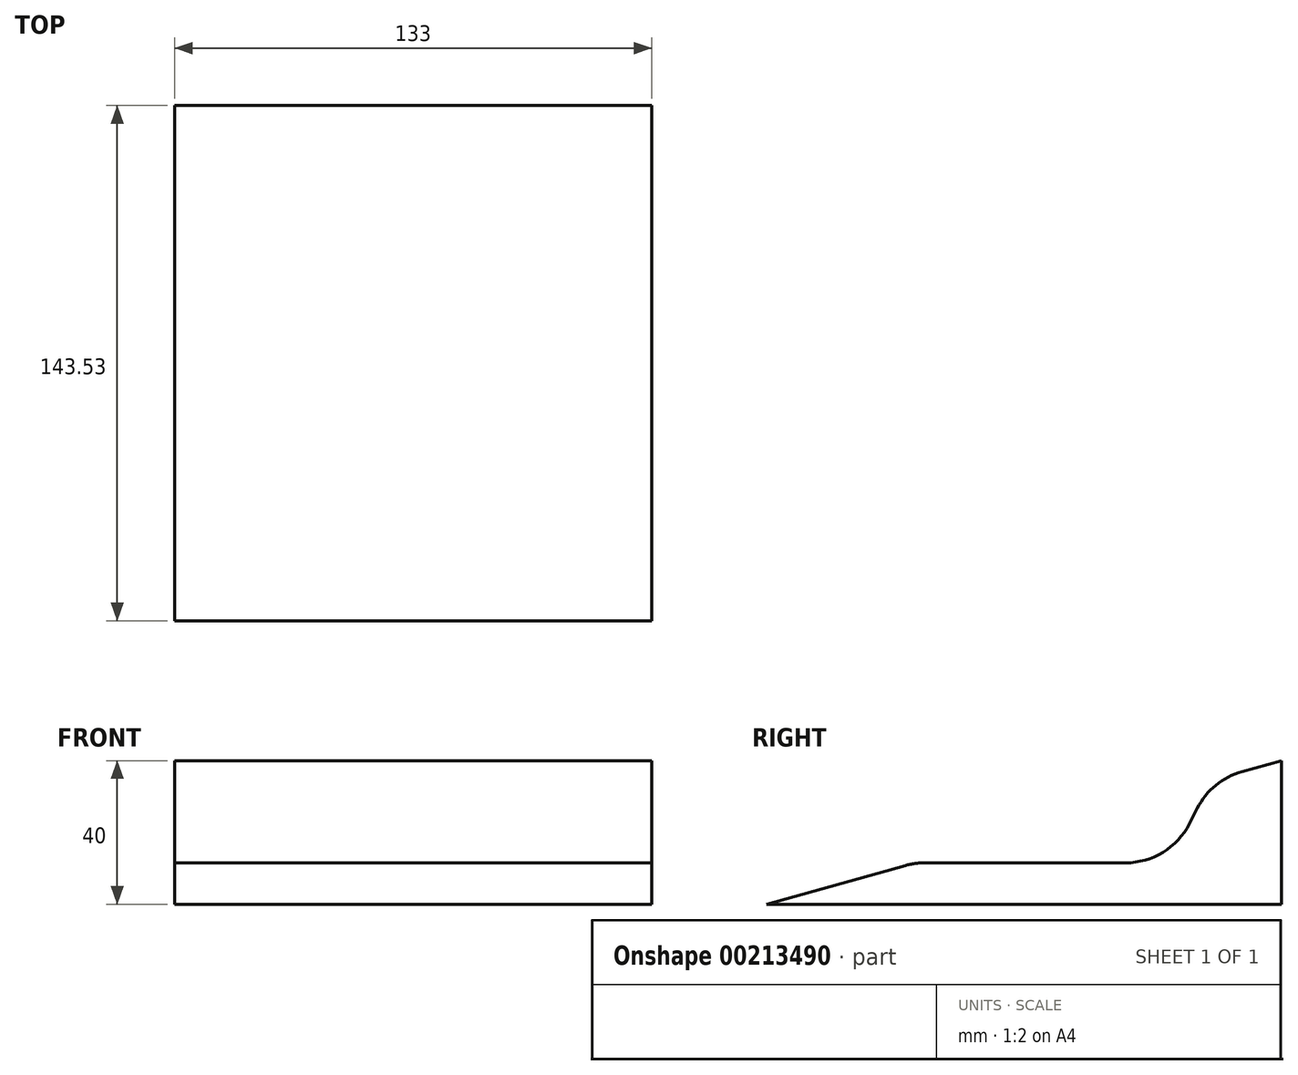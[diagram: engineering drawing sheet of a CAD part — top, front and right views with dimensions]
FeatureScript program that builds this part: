
annotation { "Feature Type Name" : "Feature", "Feature Type Description" : "" }
export const myFeature = defineFeature(function(context is Context, id is Id, definition is map)
    precondition{}
    {
        {
            var Q0;
            Q0=qCreatedBy(makeId("Right.planeOp"),FACE);
            var sketch = newSketch(context, id + "F0", { "sketchPlane" : qUnion([Q0])});
            skLineSegment(sketch, "E0", {"start": v(-72.82, -21.05) * mm, "end": v(70.71, -21.05) * mm});
            skLineSegment(sketch, "E1", {"start": v(70.71, -21.05) * mm, "end": v(70.71, 18.95) * mm});
            skLineSegment(sketch, "E2", {"start": v(70.71, 18.95) * mm, "end": v(-72.82, -21.05) * mm, "construction": true});
            skLineSegment(sketch, "E3", {"start": v(-72.82, -21.05) * mm, "end": v(-31.49, -9.53) * mm});
            skLineSegment(sketch, "E4", {"start": v(-31.49, -9.53) * mm, "end": v(39.48, -9.53) * mm});
            skLineSegment(sketch, "E5", {"start": v(39.48, -9.53) * mm, "end": v(51.23, 13.52) * mm});
            skLineSegment(sketch, "E6", {"start": v(51.23, 13.52) * mm, "end": v(70.71, 18.95) * mm});
            skSolve(sketch);
        }
        {
            var Q0;
            Q0 = qSketchRegion(id + "F0", true);
            extrude(context, id + "F1", {"entities" : qUnion([Q0]), "depth" : (127 + 6) * mm});
        }
        {
            var Q0;
            Q0=makeQuery(id+"F1.opExtrude","SWEPT_EDGE",EDGE,{"disambiguationData":[OSD([sQuery(id+"F0.wireOp",EDGE,"E4"),sQuery(id+"F0.wireOp",EDGE,"E5")])]});
            var Q1;
            Q1=makeQuery(id+"F1.opExtrude","SWEPT_EDGE",EDGE,{"disambiguationData":[OSD([sQuery(id+"F0.wireOp",EDGE,"E3"),sQuery(id+"F0.wireOp",EDGE,"E4")])]});
            var Q2;
            Q2=makeQuery(id+"F1.opExtrude","SWEPT_EDGE",EDGE,{"disambiguationData":[OSD([sQuery(id+"F0.wireOp",EDGE,"E5"),sQuery(id+"F0.wireOp",EDGE,"E6")])]});
            fillet(context, id + "F2", {"entities" : qUnion([Q0, Q1, Q2]), "radius" : 20 * mm, "tangentPropagation" : true, "allowEdgeOverflow" : false});
        }
    });
